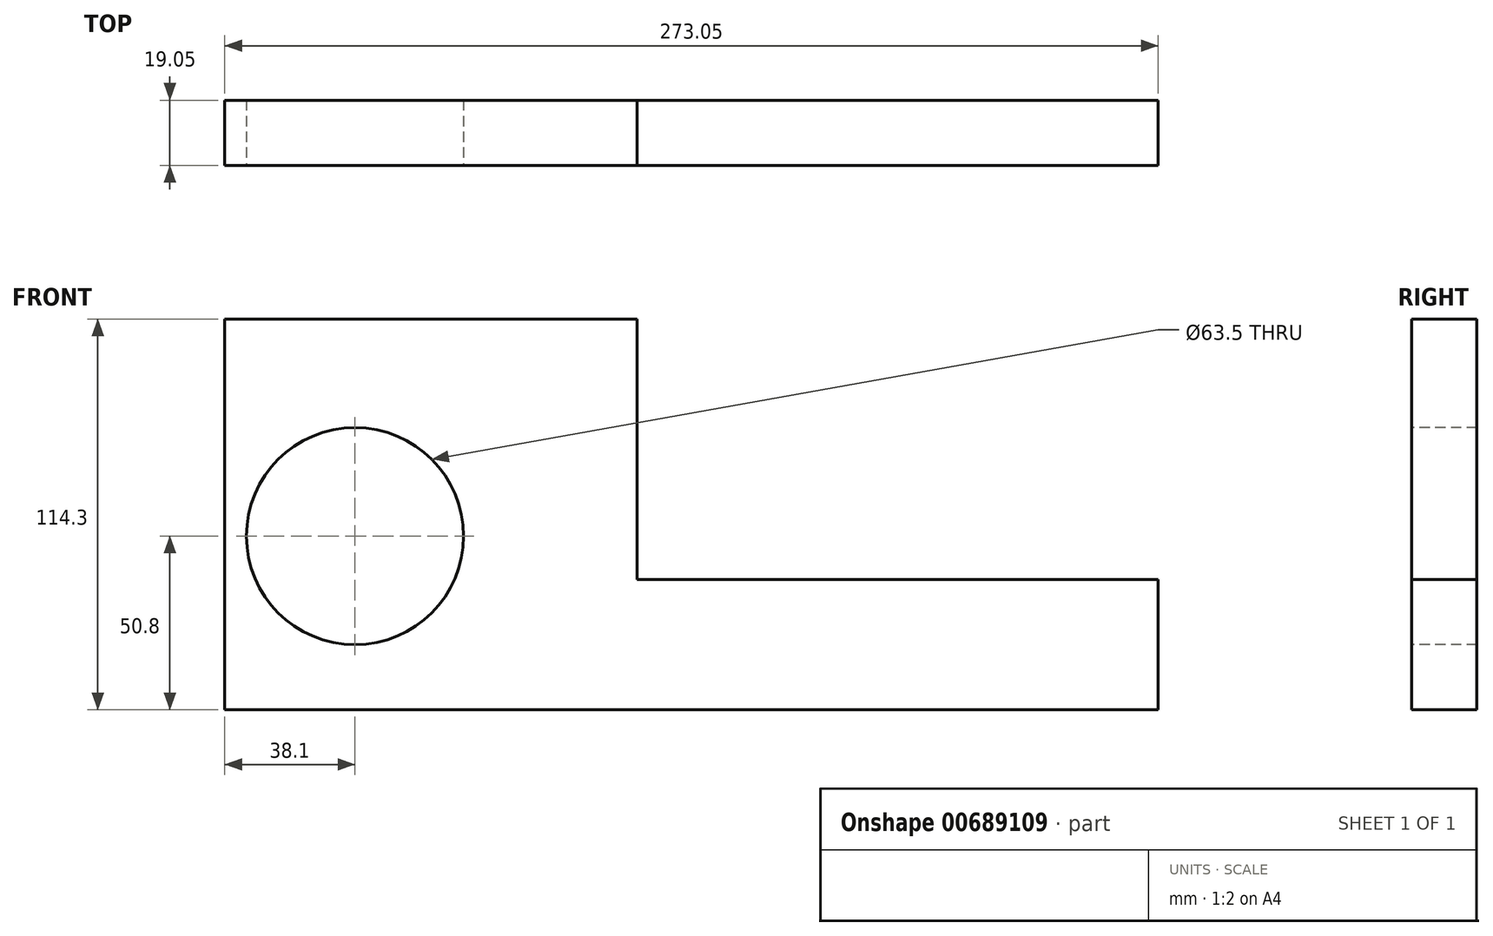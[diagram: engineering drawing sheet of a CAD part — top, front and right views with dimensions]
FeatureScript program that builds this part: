
annotation { "Feature Type Name" : "Feature", "Feature Type Description" : "" }
export const myFeature = defineFeature(function(context is Context, id is Id, definition is map)
    precondition{}
    {
        {
            var Q0;
            Q0=qCreatedBy(makeId("Front.planeOp"),FACE);
            var sketch = newSketch(context, id + "F0", { "sketchPlane" : qUnion([Q0])});
            skLineSegment(sketch, "E0.bottom", {"start": v(0, 0) * mm, "end": v(273.05, 0) * mm});
            skLineSegment(sketch, "E0.top", {"start": v(0, 114.3) * mm, "end": v(273.05, 114.3) * mm});
            skLineSegment(sketch, "E0.left", {"start": v(0, 0) * mm, "end": v(0, 114.3) * mm});
            skLineSegment(sketch, "E0.right", {"start": v(273.05, 0) * mm, "end": v(273.05, 114.3) * mm});
            skSolve(sketch);
        }
        {
            var Q0;
            Q0 = qSketchRegion(id + "F0", true);
            extrude(context, id + "F1", {"entities" : qUnion([Q0]), "depth" : 19.05 * mm, "offsetDistance" : 25.4 * mm});
        }
        {
            var Q0;
            Q0=makeQuery(id+"F1.opExtrude","CAP_FACE",FACE,{"disambiguationData":[OSD([sQuery(id+"F0.wireOp",EDGE,"E0.bottom"),sQuery(id+"F0.wireOp",EDGE,"E0.top"),sQuery(id+"F0.wireOp",EDGE,"E0.left"),sQuery(id+"F0.wireOp",EDGE,"E0.right")])],"isStart":false});
            var sketch = newSketch(context, id + "F2", { "sketchPlane" : qUnion([Q0])});
            skCircle(sketch, "E1", {"center": v(38.1, 50.8) * mm, "radius": 31.75 * mm});
            skSolve(sketch);
        }
        {
            var Q0;
            Q0=makeQuery(id+"F2.imprint","IMPRINT",FACE,{"disambiguationData":[TD([[makeQuery(id+"F2.imprint","IMPRINT",EDGE,{"derivedFrom":sQuery(id+"F2.wireOp",EDGE,"E1")}),1.0]])]});
            extrude(context, id + "F3", {"entities" : qUnion([Q0]), "operationType" : NewBodyOperationType.REMOVE, "oppositeDirection" : true, "depth" : 25.4 * mm, "offsetDistance" : 25.4 * mm});
        }
        {
            var Q0;
            Q0=makeQuery(id+"F1.opExtrude","CAP_FACE",FACE,{"disambiguationData":[OSD([sQuery(id+"F0.wireOp",EDGE,"E0.bottom"),sQuery(id+"F0.wireOp",EDGE,"E0.top"),sQuery(id+"F0.wireOp",EDGE,"E0.left"),sQuery(id+"F0.wireOp",EDGE,"E0.right")])],"isStart":false});
            var sketch = newSketch(context, id + "F4", { "sketchPlane" : qUnion([Q0])});
            skLineSegment(sketch, "E2", {"start": v(273.05, 38.1) * mm, "end": v(120.65, 38.1) * mm});
            skLineSegment(sketch, "E3", {"start": v(120.65, 38.1) * mm, "end": v(120.65, 114.3) * mm});
            skLineSegment(sketch, "E4", {"start": v(120.65, 114.3) * mm, "end": v(273.05, 114.3) * mm});
            skLineSegment(sketch, "E5", {"start": v(273.05, 114.3) * mm, "end": v(273.05, 38.1) * mm});
            skSolve(sketch);
        }
        {
            var Q0;
            Q0=makeQuery(id+"F4.imprint","IMPRINT",FACE,{"disambiguationData":[TD([[makeQuery(id+"F4.imprint","IMPRINT",EDGE,{"derivedFrom":sQuery(id+"F4.wireOp",EDGE,"E2")}),-1.0]])]});
            extrude(context, id + "F5", {"entities" : qUnion([Q0]), "operationType" : NewBodyOperationType.REMOVE, "oppositeDirection" : true, "depth" : 25.4 * mm, "offsetDistance" : 25.4 * mm});
        }
    });
